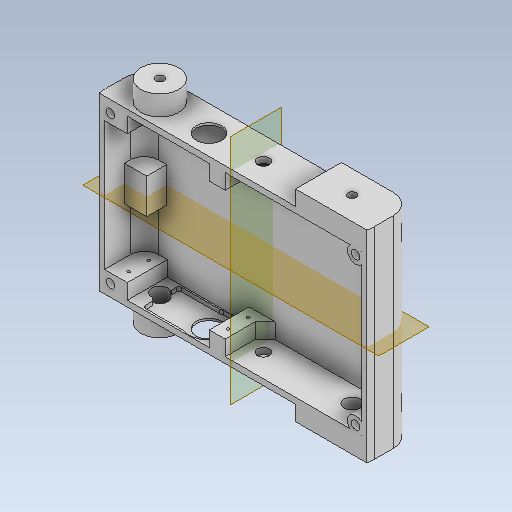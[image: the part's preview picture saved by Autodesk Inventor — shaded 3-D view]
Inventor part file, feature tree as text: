
AUTODESK INVENTOR PART (.ipt)
format: ipt  version: 2020 (Build 240168000, 168)  size: 532,992 bytes
history: native  units: mm
features: reference x30, extrude x17, sketch x14, other x12, mirror x7, hole x3, projected_geometry x3, chamfer x1
ambient origin geometry x8: Origin, YZ Plane, XZ Plane, XY Plane, X Axis, Y Axis, Z Axis, Center Point
bodies: Body1 (feature_tree)
feature tree (87):
  other  "Bryła1"
  sketch  "Szkic1"
  extrude  "Wyciągnięcie proste1"  Depth=86.0mm
  extrude  "Wyciągnięcie proste2"  Depth=135.0mm
  hole  "Otwór1"  [1 undecoded]
  sketch  "Szkic3"
  extrude  "Wyciągnięcie proste3"  Depth=3.0mm TaperAngle=0.0deg
  extrude  "Wyciągnięcie proste4"  Depth=20.0mm TaperAngle=0.0deg
  other  "Płaszczyzna konstrukcyjna1"
  mirror  "Odbij1"
  other  "Płaszczyzna konstrukcyjna2"
  sketch  "Szkic4"
  extrude  "Wyciągnięcie proste5"  Depth=96.5mm
  extrude  "Wyciągnięcie proste6"  Depth=0.5mm
  mirror  "Odbij2"
  extrude  "Wyciągnięcie proste7"  Depth=10.0mm TaperAngle=0.0deg
  extrude  "Wyciągnięcie proste8"  Depth=7.6mm TaperAngle=0.0deg
  mirror  "Odbij3"
  sketch  "Szkic7"
  extrude  "Wyciągnięcie proste9"  Depth=8.0mm
  extrude  "Wyciągnięcie proste10"  Depth=8.0mm
  chamfer  "Faza1"  Distance=10.0mm
  hole  "Otwór2"  [1 undecoded]
  mirror  "Odbij4"
  sketch  "Szkic10"
  extrude  "Wyciągnięcie proste11"  Depth=0.25mm
  extrude  "Wyciągnięcie proste12"  Depth=0.25mm
  hole  "Otwór3"  [1 undecoded]
  mirror  "Odbij5"
  other  "Płaszczyzna konstrukcyjna3"
  mirror  "Odbij6"
  sketch  "Szkic13"
  extrude  "Wyciągnięcie proste14"  Depth=2.5mm TaperAngle=0.0deg
  extrude  "Wyciągnięcie proste15"  Depth=0.25mm
  extrude  "Wyciągnięcie proste16"  Depth=0.25mm
  extrude  "Wyciągnięcie proste17"  Depth=0.25mm
  extrude  "Wyciągnięcie proste18"  Depth=0.25mm
  mirror  "Odbij7"
  sketch  "Szkic2"
  projected_geometry  "Pętla rzutowana1"
  reference  "Odniesienie1"
  sketch  "Szkic5"
  reference  "Odniesienie2"
  reference  "Odniesienie3"
  sketch  "Szkic6"
  reference  "Odniesienie4"
  reference  "Odniesienie5"
  reference  "Odniesienie6"
  reference  "Odniesienie7"
  reference  "Odniesienie8"
  reference  "Odniesienie9"
  reference  "Odniesienie10"
  reference  "Odniesienie11"
  reference  "Odniesienie12"
  reference  "Odniesienie13"
  reference  "Odniesienie14"
  reference  "Odniesienie15"
  reference  "Odniesienie16"
  reference  "Odniesienie17"
  reference  "Odniesienie18"
  reference  "Odniesienie19"
  reference  "Odniesienie20"
  reference  "Odniesienie21"
  reference  "Odniesienie22"
  reference  "Odniesienie23"
  reference  "Odniesienie24"
  sketch  "Szkic9"
  reference  "Odniesienie25"
  reference  "Odniesienie26"
  reference  "Odniesienie27"
  reference  "Odniesienie28"
  sketch  "Szkic11"
  projected_geometry  "Pętla rzutowana2"
  sketch  "Szkic14"
  sketch  "Szkic15"
  reference  "Odniesienie29"
  reference  "Odniesienie30"
  sketch  "Szkic16"
  projected_geometry  "Pętla rzutowana4"
  other  "<userpath>\Desktop\ScanBot\3d-model\Assembly1.iam"
  other  "Assembly1.iam"
  other  "wheel_MIR:1"
  other  "MG_996R:2"
  other  "Top:1"
  other  "MG_996R:1"
  other  "Medio:1"
  other  "cover-new:1"
note: 3 required parameter values undecoded (feature->parameter linkage not recoverable at this tier; creation-order binding heuristic only, values carry confidence <= 0.55)
